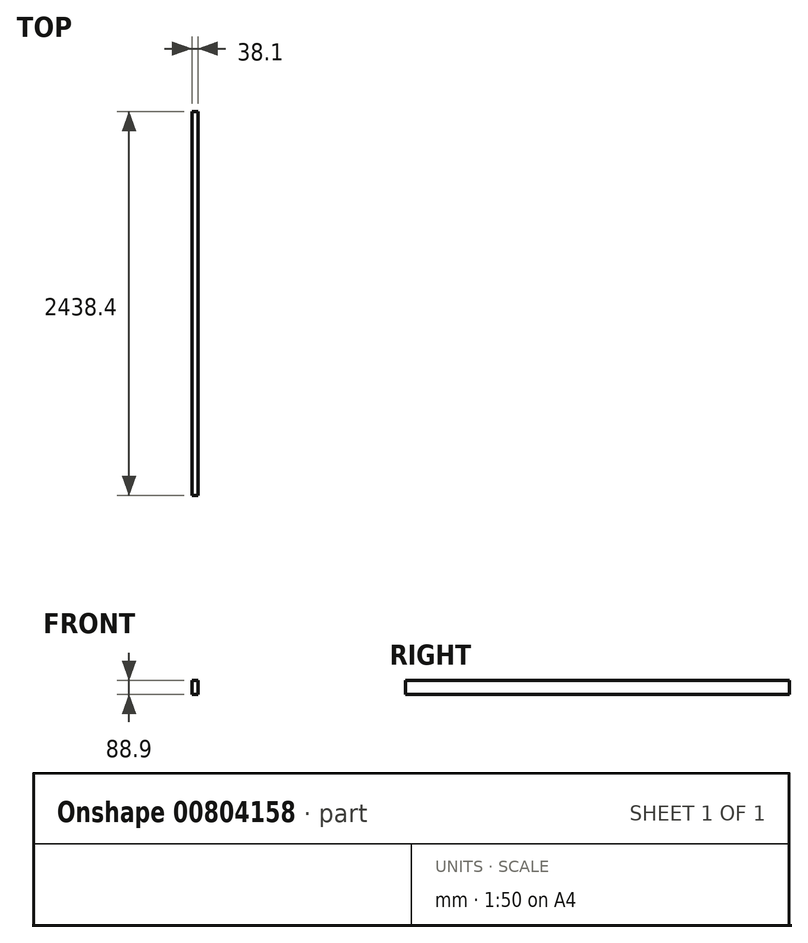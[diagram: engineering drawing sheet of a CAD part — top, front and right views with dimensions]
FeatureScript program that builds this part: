
annotation { "Feature Type Name" : "Feature", "Feature Type Description" : "" }
export const myFeature = defineFeature(function(context is Context, id is Id, definition is map)
    precondition{}
    {
        {
            var Q0;
            Q0=qCreatedBy(makeId("Front.planeOp"),FACE);
            var sketch = newSketch(context, id + "F0", { "sketchPlane" : qUnion([Q0])});
            skLineSegment(sketch, "E0.bottom", {"start": v(19.05, -44.45) * mm, "end": v(-19.05, -44.45) * mm});
            skLineSegment(sketch, "E0.top", {"start": v(19.05, 44.45) * mm, "end": v(-19.05, 44.45) * mm});
            skLineSegment(sketch, "E0.left", {"start": v(19.05, -44.45) * mm, "end": v(19.05, 44.45) * mm});
            skLineSegment(sketch, "E0.right", {"start": v(-19.05, -44.45) * mm, "end": v(-19.05, 44.45) * mm});
            skPoint(sketch, "E0.middle", {"position": v(0, 0) * mm});
            skSolve(sketch);
        }
        {
            var Q0;
            Q0 = qSketchRegion(id + "F0", true);
            extrude(context, id + "F1", {"entities" : qUnion([Q0]), "endBound" : BoundingType.SYMMETRIC, "depth" : 2438.4 * mm, "offsetDistance" : 25.4 * mm});
        }
    });
